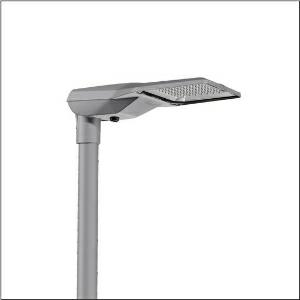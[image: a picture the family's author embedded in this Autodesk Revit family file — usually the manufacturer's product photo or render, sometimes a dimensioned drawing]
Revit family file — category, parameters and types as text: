
# Revit family: streetlight_sl_21_iq_midi___st1_0ab_5xe3m31u08mb_758c
name_source: partatom
category: Lighting Fixtures
units: mm (PartAtom-declared; Revit-internal decimal feet)

## family parameters
Cut with Voids When Loaded = No
Host = Face
Light Source = No
Part Type = Normal
Room Calculation Point = No
Round Connector Dimension = Use Diameter
Shared = No

## types (1)
- --- (1 x LED, 16140 lm, 129.3 W, 3000K)
    Apparent Load = 129 VA
    CIE Flux Codes = 38 73 97 100 100
    Color Rendering = 70
    Color Temperature = 3000K
    Default Elevation = 1800 mm
    Description = Streetlight SL 21 iQ midi, mast luminaire, primary light control with lens, of PMMA, primary optical cover: cover, of toughened safety glass, transparent, light distribution: ST1.0aB, light emission: direct distribution, primary light characteristic: asymmetric, installation type: post-top, side-entry, LED, High Power LED, rated luminous flux: 16.140lm, luminous efficacy: 125lm/W, light colour: 730, colour temperature: 3000K, control gear: iQ-Street Remote, D4i with power reduction, control: pre-setting: logarithmic dimming characteristic, Street-Remote, Auto-Match, Temp-Guard, Lumen-Switch, Night-Set, Smart-Wire, Light-Fading, Desk-Remote (wireless, voltage-free reading and setting of iQ features in the workshop via application-optimized NFC function/RFID function), optimised constant luminous flux control (CLO 2.0), mains connection: 230..240V, AC, 50/60Hz, start of lifetime: 129W, end of service life: 142W, reduction: 56W, luminaire housing, of diecast aluminium, powder-coated, SITECO metallic grey (DB 702S), corrosivity category C5 high according to DIN EN ISO 12944, please order mast flange separately, inclination adjustable: 0°, 5°, 10°, 15°, sealing non-destructively replaceable, multi-level sealing system, length: 644mm, width: 335mm, height: 110mm, mast flange for spigot size: 42mm (side-entry): 5XC10008XM4, 60/48mm (side-entry/post-top): 5XC10108XM2, 76/60mm (side-entry/post-top): 5XC10108XM1, mounting height: 4..8m, Smart Interface below, protection rating (complete): IP66, insulation class (complete): insulation class II (safety insulation), certification: CE, ENEC, ENEC+, VDE, impact resistance: IK10, permissible operating ambient temperature for outdoor applications: -40..+50°C, standard-compliant lighting for roads and squares, packaging unit: 1 piece

Light Distribution: ST1.0aB
    Height = 111 mm
    Lamp = 1 x LED
    Lamp Light Flux = 16140 lm
    Lamp Power = 129.3 W
    Lamp count = 1
    Length = 644 mm
    Luminous efficacy = 125 lm/W
    Manufacturer = Siteco
    ModVariant = No
    Model = 5XE3M31U08MB
    Number of Poles = 1
    OnlyDefault = Yes
    Power Factor = 1
    Product Name = Streetlight SL 21 iQ midi | ST1.0aB
    Product group = mast luminaire | pylon top
    ProductGroupID = 6100
    Protection Class = Protection class II
    Protection Degree = IP 66
    RLX_Detail_Level = 1
    RLX_Emergency_Light_Flux = 0 lm
    RLX_Emergency_Type = 0
    RLX_Emergency_Type_DB = No
    RlxData = <blob elided: 90929 chars, md5=1f3ea333>
    Socket = socket
    Standby Power = 0 W
    System Light Flux = 16141 lm
    System Power = 129 W
    Type Comments = factory setting: luminous flux: 100 % | dim-lin: 254 | 672 mA
    Type Image = l_1004300.jpg
    URL = http://relux.com
    VarID = @adj_112353
    Voltage = 0 V
    Weight = 0.00 kg
    Width = 336 mm

## geometry (parser evidence)
native form markers: Blend x4, Sweep x12
no freeform markers — native parametric forms only
